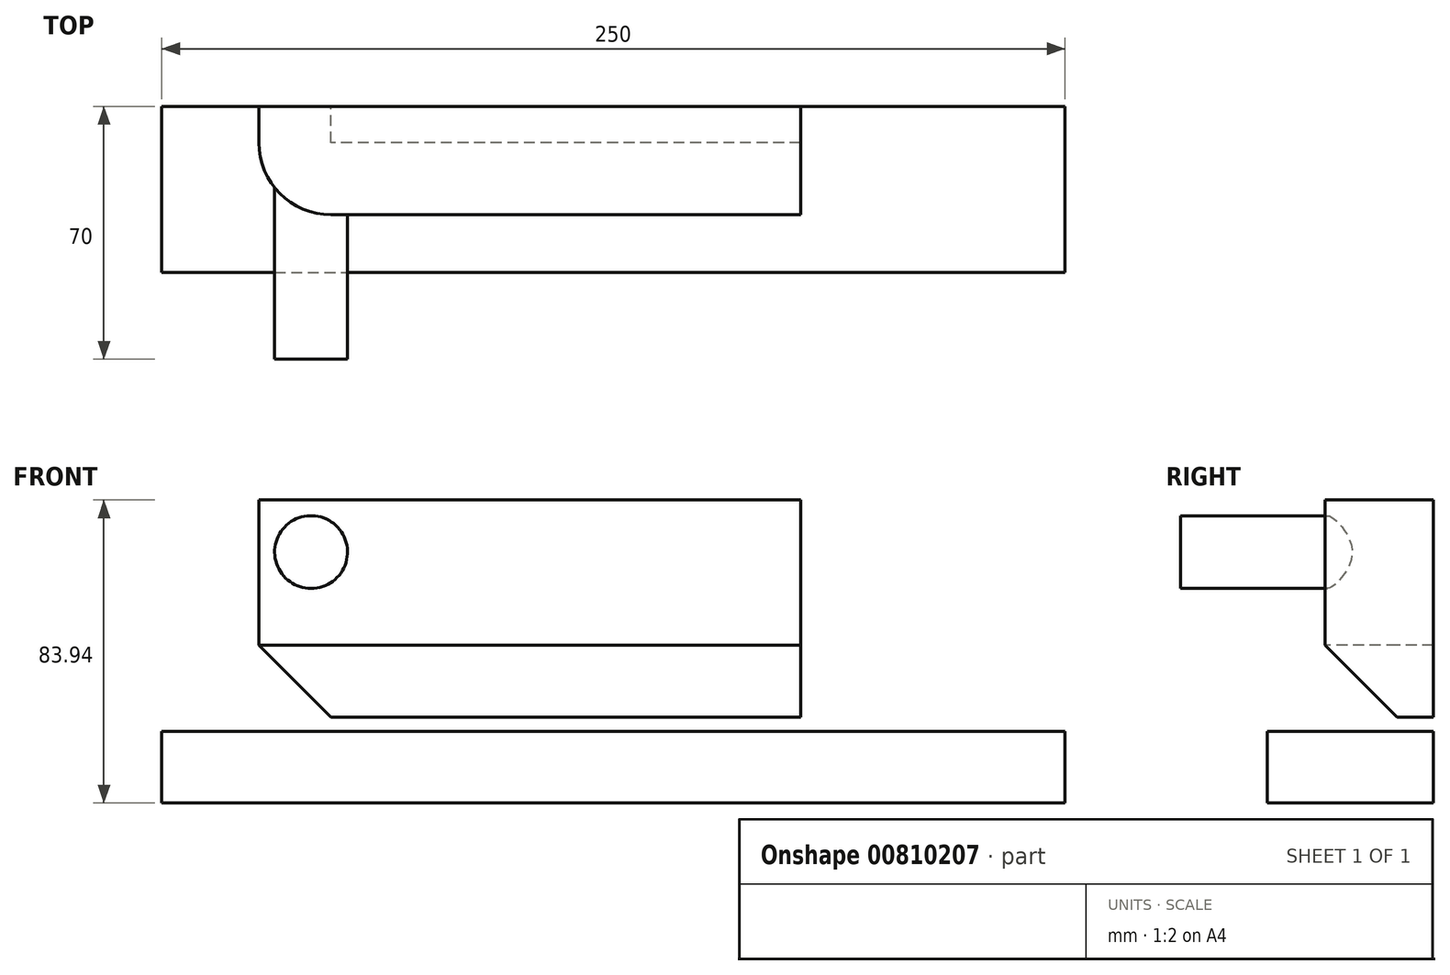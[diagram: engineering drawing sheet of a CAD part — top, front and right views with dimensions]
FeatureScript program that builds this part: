
annotation { "Feature Type Name" : "Feature", "Feature Type Description" : "" }
export const myFeature = defineFeature(function(context is Context, id is Id, definition is map)
    precondition{}
    {
        {
            var Q0;
            Q0=qCreatedBy(makeId("Front.planeOp"),FACE);
            var sketch = newSketch(context, id + "F0", { "sketchPlane" : qUnion([Q0])});
            skLineSegment(sketch, "E0.bottom", {"start": v(-85.91, 33.1) * mm, "end": v(64.09, 33.1) * mm});
            skLineSegment(sketch, "E0.top", {"start": v(-85.91, -27.1) * mm, "end": v(64.09, -27.1) * mm});
            skLineSegment(sketch, "E0.left", {"start": v(-85.91, 33.1) * mm, "end": v(-85.91, -27.1) * mm});
            skLineSegment(sketch, "E0.right", {"start": v(64.09, 33.1) * mm, "end": v(64.09, -27.1) * mm});
            skCircle(sketch, "E1", {"center": v(-71.46, 18.67) * mm, "radius": 10.08 * mm});
            skLineSegment(sketch, "E2.bottom", {"start": v(-112.77, -31.04) * mm, "end": v(137.23, -31.04) * mm});
            skLineSegment(sketch, "E2.top", {"start": v(-112.77, -50.83) * mm, "end": v(137.23, -50.83) * mm});
            skLineSegment(sketch, "E2.left", {"start": v(-112.77, -31.04) * mm, "end": v(-112.77, -50.83) * mm});
            skLineSegment(sketch, "E2.right", {"start": v(137.23, -31.04) * mm, "end": v(137.23, -50.83) * mm});
            skText(sketch, "E3", { "text": "2016/17", "fontName": "OpenSans-Bold.ttf"});
            const initialGuessF0  = {"E3": [-0.11277, 0.03793, 1, 0, 0.04211]};
            skSetInitialGuess(sketch, initialGuessF0);
            skSolve(sketch);
        }
        {
            var Q0;
            Q0=makeQuery(id+"F0.imprint","IMPRINT",FACE,{"disambiguationData":[TD([[makeQuery(id+"F0.imprint","IMPRINT",EDGE,{"derivedFrom":sQuery(id+"F0.wireOp",EDGE,"E0.bottom")}),-1.0]])]});
            extrude(context, id + "F1", {"entities" : qUnion([Q0]), "depth" : 30 * mm, "offsetDistance" : 25 * mm});
        }
        {
            var Q0;
            Q0=makeQuery(id+"F0.imprint","IMPRINT",FACE,{"disambiguationData":[TD([[makeQuery(id+"F0.imprint","IMPRINT",EDGE,{"derivedFrom":sQuery(id+"F0.wireOp",EDGE,"E1")}),1.0]])]});
            extrude(context, id + "F2", {"entities" : qUnion([Q0]), "operationType" : NewBodyOperationType.ADD, "depth" : 70 * mm, "offsetDistance" : 25 * mm});
        }
        {
            var Q0;
            Q0=makeQuery(id+"F1.opExtrude","CAP_EDGE",EDGE,{"disambiguationData":[OSD([sQuery(id+"F0.wireOp",EDGE,"E0.left")])],"isStart":false});
            fillet(context, id + "F3", {"entities" : qUnion([Q0]), "radius" : 20 * mm, "tangentPropagation" : true, "allowEdgeOverflow" : false});
        }
        {
            var Q0;
            Q0=makeQuery(id+"F1.opExtrude","CAP_EDGE",EDGE,{"disambiguationData":[OSD([sQuery(id+"F0.wireOp",EDGE,"E0.top")])],"isStart":false});
            chamfer(context, id + "F4", {"entities" : qUnion([Q0]), "width" : 20 * mm, "tangentPropagation" : true});
        }
        {
            var Q0;
            Q0=makeQuery(id+"F0.imprint","IMPRINT",FACE,{"disambiguationData":[TD([[makeQuery(id+"F0.imprint","IMPRINT",EDGE,{"derivedFrom":sQuery(id+"F0.wireOp",EDGE,"E2.bottom")}),-1.0]])]});
            extrude(context, id + "F5", {"entities" : qUnion([Q0]), "operationType" : NewBodyOperationType.ADD, "depth" : 46 * mm, "offsetDistance" : 25 * mm});
        }
    });
